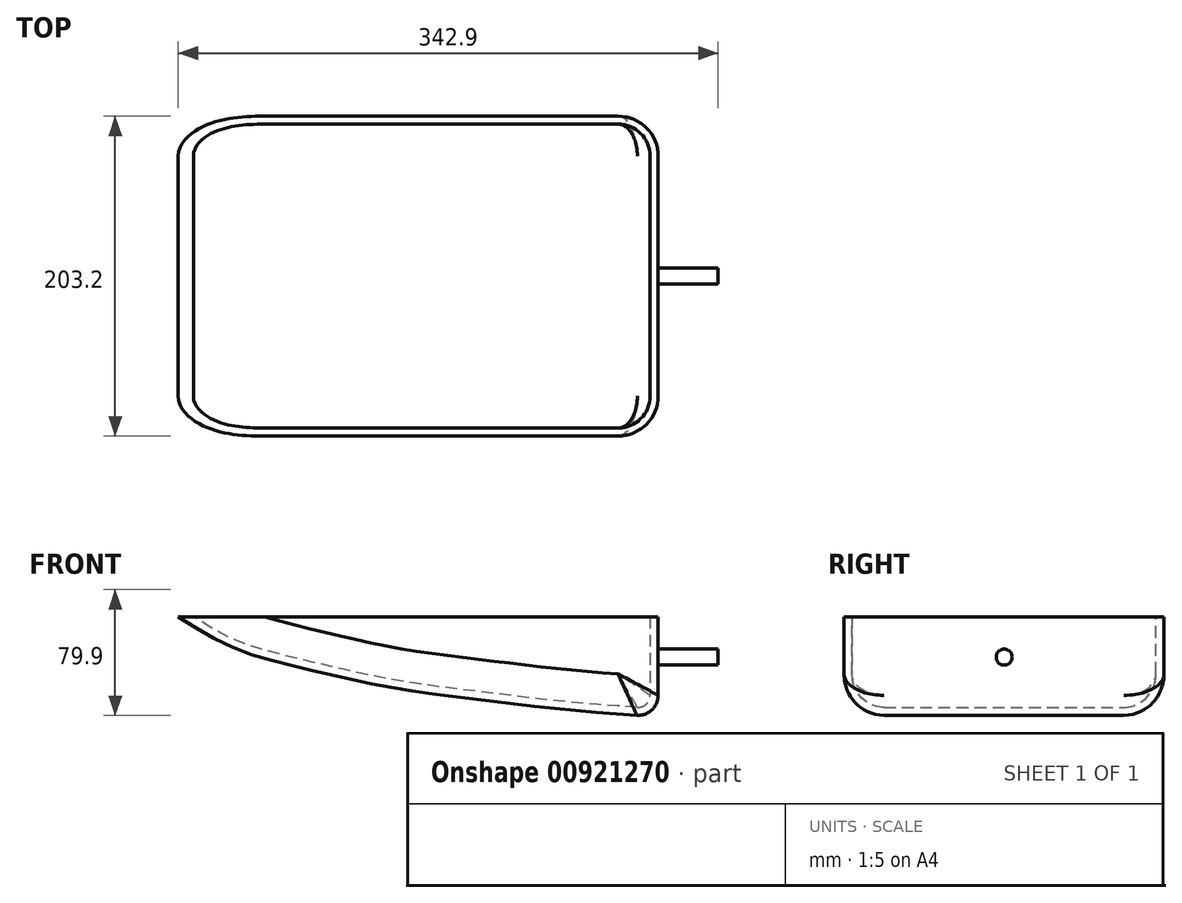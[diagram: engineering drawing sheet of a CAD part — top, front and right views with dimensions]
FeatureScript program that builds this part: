
annotation { "Feature Type Name" : "Feature", "Feature Type Description" : "" }
export const myFeature = defineFeature(function(context is Context, id is Id, definition is map)
    precondition{}
    {
        {
            var Q0;
            Q0=qCreatedBy(makeId("Front.planeOp"),FACE);
            var sketch = newSketch(context, id + "F0", { "sketchPlane" : qUnion([Q0])});
            skLineSegment(sketch, "E0", {"start": v(-179.87, 12.81) * mm, "end": v(124.93, 12.81) * mm});
            skLineSegment(sketch, "E1", {"start": v(124.93, 12.81) * mm, "end": v(124.93, -37.16) * mm});
            skFitSpline(sketch, "E2", {"points": [v(-179.87, 12.81) * mm, v(-152.3, -3.53) * mm, v(-124.84, -13.75) * mm, v(-86.88, -23.1) * mm, v(-41.6, -32.74) * mm, v(17.1, -40.62) * mm, v(62.07, -45.88) * mm, v(109.08, -49.67) * mm, v(124.93, -50.69) * mm], "startDerivative": vector(243.6, -150.08) * mm, "endDerivative": vector(166.99, -10.76) * mm});
            skFitSpline(sketch, "E3", {"points": [v(124.93, 12.81) * mm, v(129.6, -8.5) * mm, v(129.02, -29.23) * mm, v(124.93, -50.69) * mm], "startDerivative": vector(28.37, -48.83) * mm, "endDerivative": vector(-24.98, -112.37) * mm, "construction": true});
            skArc(sketch, "E4.filletArc", {"start": v(111.4, -49.83) * mm, "mid": v(120.91, -46.43) * mm, "end": v(124.93, -37.16) * mm});
            skSolve(sketch);
        }
        {
            var Q0;
            Q0=qSketchRegion(id+"F0",true);
            extrude(context, id + "F1", {"entities" : qUnion([Q0]), "depth" : 203.2 * mm, "offsetDistance" : 25.4 * mm});
        }
        {
            var Q0;
            Q0=makeQuery(id+"F1.opExtrude","CAP_EDGE",EDGE,{"disambiguationData":[OSD([sQuery(id+"F0.wireOp",EDGE,"E1")])],"isStart":false});
            var Q1;
            Q1=makeQuery(id+"F1.opExtrude","CAP_EDGE",EDGE,{"disambiguationData":[OSD([sQuery(id+"F0.wireOp",EDGE,"E1")])],"isStart":true});
            fillet(context, id + "F2", {"entities" : qUnion([Q0, Q1]), "radius" : 25.4 * mm, "tangentPropagation" : true, "allowEdgeOverflow" : false});
        }
        {
            var Q0;
            {var subQ0=sQuery(id+"F0.wireOp",EDGE,"E1");Q0=makeQuery(id+"F2.opFillet","BLEND_VERTEX",VERTEX,{"blendedFrom":[makeQuery(id+"F1.opExtrude","CAP_EDGE",EDGE,{"disambiguationData":[OSD([subQ0])],"isStart":false}),makeQuery(id+"F1.opExtrude","SWEPT_FACE",FACE,{"disambiguationData":[OSD([subQ0])]}),makeQuery(id+"F1.opExtrude","SWEPT_FACE",FACE,{"disambiguationData":[OSD([sQuery(id+"F0.wireOp",EDGE,"E0")])]})],"blendedInto":[makeQuery(id+"F1.opExtrude","SWEPT_FACE",FACE,{"disambiguationData":[OSD([subQ0])]}),makeQuery(id+"F1.opExtrude","SWEPT_FACE",FACE,{"disambiguationData":[OSD([sQuery(id+"F0.wireOp",EDGE,"E0")])]})]});}
            var Q1;
            {var subQ0=sQuery(id+"F0.wireOp",EDGE,"E4.filletArc");var subQ1=sQuery(id+"F0.wireOp",EDGE,"E1");Q1=makeQuery(id+"F2.opFillet","BLEND_VERTEX",VERTEX,{"blendedFrom":[makeQuery(id+"F1.opExtrude","CAP_EDGE",EDGE,{"disambiguationData":[OSD([subQ1])],"isStart":false}),makeQuery(id+"F1.opExtrude","CAP_EDGE",EDGE,{"disambiguationData":[OSD([subQ0])],"isStart":false}),makeQuery(id+"F1.opExtrude","SWEPT_FACE",FACE,{"disambiguationData":[OSD([subQ1])]}),makeQuery(id+"F1.opExtrude","SWEPT_FACE",FACE,{"disambiguationData":[OSD([subQ0])]})],"blendedInto":[makeQuery(id+"F1.opExtrude","SWEPT_FACE",FACE,{"disambiguationData":[OSD([subQ1])]}),makeQuery(id+"F1.opExtrude","SWEPT_FACE",FACE,{"disambiguationData":[OSD([subQ0])]})]});}
            var Q2;
            {var subQ0=sQuery(id+"F0.wireOp",EDGE,"E4.filletArc");var subQ1=sQuery(id+"F0.wireOp",EDGE,"E1");Q2=makeQuery(id+"F2.opFillet","BLEND_VERTEX",VERTEX,{"blendedFrom":[makeQuery(id+"F1.opExtrude","CAP_EDGE",EDGE,{"disambiguationData":[OSD([subQ1])],"isStart":true}),makeQuery(id+"F1.opExtrude","CAP_EDGE",EDGE,{"disambiguationData":[OSD([subQ0])],"isStart":true}),makeQuery(id+"F1.opExtrude","SWEPT_FACE",FACE,{"disambiguationData":[OSD([subQ1])]}),makeQuery(id+"F1.opExtrude","SWEPT_FACE",FACE,{"disambiguationData":[OSD([subQ0])]})],"blendedInto":[makeQuery(id+"F1.opExtrude","SWEPT_FACE",FACE,{"disambiguationData":[OSD([subQ1])]}),makeQuery(id+"F1.opExtrude","SWEPT_FACE",FACE,{"disambiguationData":[OSD([subQ0])]})]});}
            cPlane(context, id + "F3", {"entities" : qUnion([Q0, Q1, Q2]), "cplaneType" : CPlaneType.THREE_POINT, "offset" : 25.4 * mm, "width" : 152.4 * mm, "height" : 152.4 * mm});
        }
        {
            var Q0;
            Q0=qCreatedBy(id+"F3.planeOp",FACE);
            var sketch = newSketch(context, id + "F4", { "sketchPlane" : qUnion([Q0])});
            skCircle(sketch, "E5", {"center": v(101.49, -12.86) * mm, "radius": 5.08 * mm});
            skLineSegment(sketch, "E6", {"start": v(101.49, 12.54) * mm, "end": v(101.49, -12.86) * mm, "construction": true});
            skLineSegment(sketch, "E7", {"start": v(25.33, -10.31) * mm, "end": v(101.49, -12.86) * mm, "construction": true});
            skSolve(sketch);
        }
        {
            var Q0;
            Q0=qSketchRegion(id+"F4",true);
            extrude(context, id + "F5", {"entities" : qUnion([Q0]), "operationType" : NewBodyOperationType.ADD, "oppositeDirection" : true, "depth" : 38.1 * mm, "offsetDistance" : 25.4 * mm});
        }
        {
            var Q0;
            Q0=makeQuery(id+"F1.opExtrude","SWEPT_FACE",FACE,{"disambiguationData":[OSD([sQuery(id+"F0.wireOp",EDGE,"E0")])]});
            shell(context, id + "F6", {"entities" : qUnion([Q0]), "thickness" : 5.08 * mm});
        }
    });
